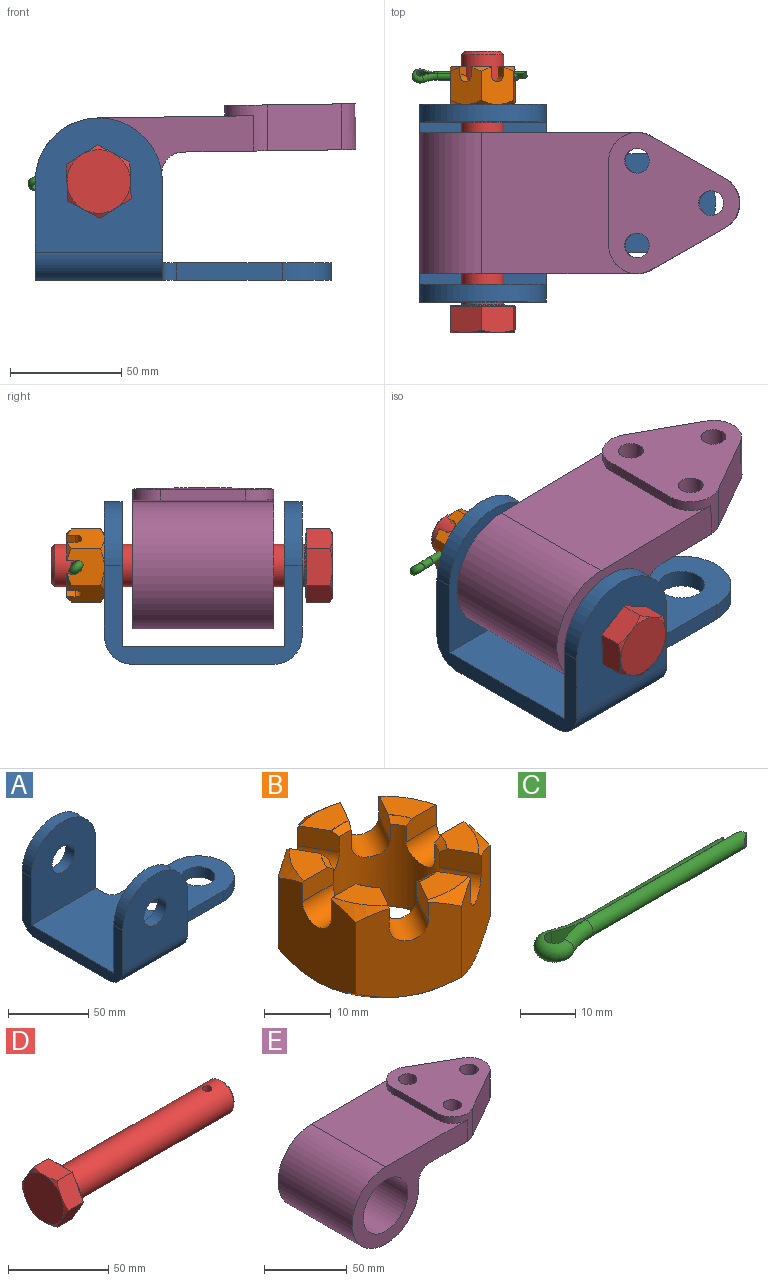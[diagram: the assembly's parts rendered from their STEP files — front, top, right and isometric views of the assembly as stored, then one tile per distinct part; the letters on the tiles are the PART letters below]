
ASSEMBLY  parts=5 mates=4
PART A: 22 faces, bbox 133.4x88.9x73 mm
  f0: plane 44.45x15.88mm, normal (1,0,0), area 381.2mm2, adj f2,f6,f7,f14,f15,f18,f21
  f1: cylinder r=9.92mm len=19.85mm, axis (0,1,0), area 494.9mm2, adj f7,f18
  f2: cylinder r=28.57mm len=57.15mm, axis (0,1,0), area 712.6mm2, adj f0,f7,f8,f18
  f3: plane 47.63x7.94mm, normal (0,-1,0), area 378mm2, adj f4,f13,f14,f15
  f4: cylinder r=22.23mm len=44.45mm, axis (0,0,-1), area 554.2mm2, adj f3,f5,f14,f15
  f5: plane 47.63x7.94mm, normal (0,1,0), area 378mm2, adj f4,f6,f14,f15
  f6: cylinder r=6.35mm len=7.94mm, axis (0,0,-1), area 79.2mm2, adj f0,f5,f14,f15
  f7: plane 60.33x57.15mm, normal (0,1,0), area 2787.8mm2, adj f0,f1,f2,f8,f21
  f8: plane 88.9x44.45mm, normal (-1,0,0), area 1216.1mm2, adj f2,f7,f9,f14,f15,f17,f18,f19
  f9: plane 60.33x57.15mm, normal (0,-1,0), area 2787.8mm2, adj f8,f10,f16,f17,f20
  f10: plane 44.45x15.88mm, normal (1,0,0), area 381.2mm2, adj f9,f13,f14,f15,f17,f19,f20
  f11: cylinder r=10.33mm len=20.65mm, axis (0,0,-1), area 514.9mm2, adj f14,f15
  f12: cylinder r=10.33mm len=20.65mm, axis (0,0,-1), area 514.9mm2, adj f14,f15
  f13: cylinder r=6.35mm len=7.94mm, axis (0,0,-1), area 79.2mm2, adj f3,f10,f14,f15
  f14: plane 133.35x73.03mm, normal (0,0,1), area 6695.9mm2, adj f0,f3,f4,f5,f6,f8,f10,f11
  f15: plane 133.35x63.5mm, normal (0,0,-1), area 6151.6mm2, adj f0,f3,f4,f5,f6,f8,f10,f11
  f16: cylinder r=9.92mm len=19.85mm, axis (0,1,0), area 494.9mm2, adj f9,f19
  f17: cylinder r=28.57mm len=57.15mm, axis (0,1,0), area 712.6mm2, adj f8,f9,f10,f19
  f18: plane 65.09x57.15mm, normal (0,-1,0), area 3060mm2, adj f0,f1,f2,f8,f14
  f19: plane 65.09x57.15mm, normal (0,1,0), area 3060mm2, adj f8,f10,f14,f16,f17
  f20: cylinder r=12.7mm len=57.15mm, axis (1,0,0), area 1140.1mm2, adj f8,f9,f10,f15
  f21: cylinder r=12.7mm len=57.15mm, axis (-1,0,0), area 1140.1mm2, adj f0,f7,f8,f15
PART B: 64 faces, bbox 33x33x16.9 mm
  f0: cylinder r=8.33mm len=16.67mm, axis (0,0,1), area 599.6mm2, adj f8,f9,f10,f11,f12,f13,f14,f15
  f1: plane 28.58x28.58mm, normal (0,0,-1), area 356.3mm2, adj f32,f33,f34,f35,f36,f37,f51
  f2: plane 8.68x4.95mm, normal (0,0,1), area 30mm2, adj f12,f16,f41,f48
  f3: plane 7.52x6.81mm, normal (0,0,1), area 30mm2, adj f9,f13,f43,f49
  f4: plane 7.52x6.81mm, normal (0,0,1), area 30mm2, adj f8,f18,f39,f44
  f5: plane 7.52x6.81mm, normal (0,0,1), area 30mm2, adj f11,f15,f42,f46
  f6: plane 7.52x6.81mm, normal (0,0,1), area 30mm2, adj f10,f17,f40,f47
  f7: plane 8.68x4.95mm, normal (0,0,1), area 30mm2, adj f14,f19,f38,f45
  f8: plane 6.56x3.71mm, normal (0,-1,0), area 23.4mm2, adj f0,f4,f22,f26,f39,f44,f62,f63
  f9: plane 6.56x3.71mm, normal (0,1,0), area 23.4mm2, adj f0,f3,f22,f26,f43,f49,f52,f53
  f10: plane 6.56x3.71mm, normal (0,1,0), area 23.4mm2, adj f0,f6,f25,f27,f40,f47,f56,f57
  f11: plane 6.56x3.71mm, normal (0,-1,0), area 23.4mm2, adj f0,f5,f25,f27,f42,f46,f58,f59
  f12: plane 5.69x3.71mm, normal (0.87,0.5,0), area 23.4mm2, adj f0,f2,f23,f28,f41,f48,f54,f55
  f13: plane 5.69x3.71mm, normal (-0.87,-0.5,0), area 23.4mm2, adj f0,f3,f23,f28,f43,f49,f52,f53
  f14: plane 5.69x3.71mm, normal (-0.87,-0.5,0), area 23.4mm2, adj f0,f7,f20,f29,f38,f45,f60,f61
  f15: plane 5.69x3.71mm, normal (0.87,0.5,0), area 23.4mm2, adj f0,f5,f20,f29,f42,f46,f58,f59
  f16: plane 5.69x3.71mm, normal (-0.87,0.5,0), area 23.4mm2, adj f0,f2,f24,f30,f41,f48,f54,f55
  f17: plane 5.69x3.71mm, normal (0.87,-0.5,0), area 23.4mm2, adj f0,f6,f24,f30,f40,f47,f56,f57
  f18: plane 5.69x3.71mm, normal (-0.87,0.5,0), area 23.4mm2, adj f0,f4,f21,f31,f39,f44,f62,f63
  f19: plane 5.69x3.71mm, normal (0.87,-0.5,0), area 23.4mm2, adj f0,f7,f21,f31,f38,f45,f60,f61
  f20: plane 16.62x14.29mm, normal (-0.5,0.87,0), area 220.6mm2, adj f14,f15,f21,f25,f29,f32,f33,f38
  f21: plane 16.62x14.29mm, normal (0.5,0.87,0), area 220.6mm2, adj f18,f19,f20,f22,f31,f33,f34,f38
  f22: plane 16.63x16.51mm, normal (1,0,0), area 220.6mm2, adj f8,f9,f21,f23,f26,f34,f35,f39
  f23: plane 16.62x14.29mm, normal (0.5,-0.87,0), area 220.6mm2, adj f12,f13,f22,f24,f28,f35,f36,f41
  f24: plane 16.62x14.29mm, normal (-0.5,-0.87,0), area 220.6mm2, adj f16,f17,f23,f25,f30,f36,f37,f40
  f25: plane 16.63x16.51mm, normal (-1,0,0), area 220.6mm2, adj f10,f11,f20,f24,f27,f32,f37,f40
  f26: cylinder r=3.05mm len=6.53mm, axis (1,0,0), area 59.8mm2, adj f0,f8,f9,f22
  f27: cylinder r=3.05mm len=6.53mm, axis (1,0,0), area 59.8mm2, adj f0,f10,f11,f25
  f28: cylinder r=3.05mm len=8.7mm, axis (-0.5,0.87,0), area 59.8mm2, adj f0,f12,f13,f23
  f29: cylinder r=3.05mm len=8.7mm, axis (-0.5,0.87,0), area 59.8mm2, adj f0,f14,f15,f20
  f30: cylinder r=3.05mm len=8.7mm, axis (0.5,0.87,0), area 59.8mm2, adj f0,f16,f17,f24
  f31: cylinder r=3.05mm len=8.7mm, axis (0.5,0.87,0), area 59.8mm2, adj f0,f18,f19,f21
  f32: cone r=14.29mm half-angle=49.2deg, axis (0,0,1), area 14.5mm2, adj f1,f20,f25
  f33: cone r=14.29mm half-angle=49.2deg, axis (0,0,1), area 14.5mm2, adj f1,f20,f21
  f34: cone r=14.29mm half-angle=49.2deg, axis (0,0,1), area 14.5mm2, adj f1,f21,f22
  f35: cone r=14.29mm half-angle=49.2deg, axis (0,0,1), area 14.5mm2, adj f1,f22,f23
  f36: cone r=14.29mm half-angle=49.2deg, axis (0,0,1), area 14.5mm2, adj f1,f23,f24
  f37: cone r=14.29mm half-angle=49.2deg, axis (0,0,1), area 14.5mm2, adj f1,f24,f25
  f38: cone r=14.29mm half-angle=49.2deg, axis (0,0,-1), area 13.6mm2, adj f7,f14,f19,f20,f21
  f39: cone r=14.29mm half-angle=49.2deg, axis (0,0,-1), area 13.6mm2, adj f4,f8,f18,f21,f22
  f40: cone r=14.29mm half-angle=49.2deg, axis (0,0,-1), area 13.6mm2, adj f6,f10,f17,f24,f25
  f41: cone r=14.29mm half-angle=49.2deg, axis (0,0,-1), area 13.6mm2, adj f2,f12,f16,f23,f24
  f42: cone r=14.29mm half-angle=49.2deg, axis (0,0,-1), area 13.6mm2, adj f5,f11,f15,f20,f25
  f43: cone r=14.29mm half-angle=49.2deg, axis (0,0,-1), area 13.6mm2, adj f3,f9,f13,f22,f23
  f44: cone r=8.21mm half-angle=55deg, axis (0,0,1), area 0.1mm2, adj f4,f8,f18,f63
  f45: cone r=8.21mm half-angle=55deg, axis (0,0,1), area 0.1mm2, adj f7,f14,f19,f60
  f46: cone r=8.21mm half-angle=55deg, axis (0,0,1), area 0.1mm2, adj f5,f11,f15,f58
  f47: cone r=8.21mm half-angle=55deg, axis (0,0,1), area 0.1mm2, adj f6,f10,f17,f56
  f48: cone r=8.21mm half-angle=55deg, axis (0,0,1), area 0.1mm2, adj f2,f12,f16,f54
  f49: cone r=8.21mm half-angle=55deg, axis (0,0,1), area 0.1mm2, adj f3,f9,f13,f52
  f50: cone r=9.53mm half-angle=55deg, axis (0,0,-1), area 81.6mm2, adj f0,f51
  f51: cylinder r=9.53mm len=19.05mm, axis (0,0,1), area 1.5mm2, adj f1,f50
  f52: cone r=9.53mm half-angle=55deg, axis (0,0,-1), area 0.1mm2, adj f9,f13,f49,f53
  f53: cone r=8.33mm half-angle=55deg, axis (0,0,1), area 4.5mm2, adj f0,f9,f13,f52
  f54: cone r=9.53mm half-angle=55deg, axis (0,0,-1), area 0.1mm2, adj f12,f16,f48,f55
  f55: cone r=8.33mm half-angle=55deg, axis (0,0,1), area 4.5mm2, adj f0,f12,f16,f54
  f56: cone r=9.53mm half-angle=55deg, axis (0,0,-1), area 0.1mm2, adj f10,f17,f47,f57
  f57: cone r=8.33mm half-angle=55deg, axis (0,0,1), area 4.5mm2, adj f0,f10,f17,f56
  f58: cone r=9.53mm half-angle=55deg, axis (0,0,-1), area 0.1mm2, adj f11,f15,f46,f59
  f59: cone r=8.33mm half-angle=55deg, axis (0,0,1), area 4.5mm2, adj f0,f11,f15,f58
  f60: cone r=9.53mm half-angle=55deg, axis (0,0,-1), area 0.1mm2, adj f14,f19,f45,f61
  f61: cone r=8.33mm half-angle=55deg, axis (0,0,1), area 4.5mm2, adj f0,f14,f19,f60
  f62: cone r=8.33mm half-angle=55deg, axis (0,0,1), area 4.5mm2, adj f0,f8,f18,f63
  f63: cone r=9.53mm half-angle=55deg, axis (0,0,-1), area 0.1mm2, adj f8,f18,f44,f62
PART C: 14 faces, bbox 52x8x3.7 mm
  f0: plane 38.67x3.7mm, normal (0,1,0), area 143.1mm2, adj f1,f2,f13
  f1: cylinder r=1.85mm len=40mm, axis (1,0,0), area 227.7mm2, adj f0,f3,f12,f13
  f2: cylinder r=16.37mm len=7.19mm, axis (0,0,-1), area 27.5mm2, adj f0,f3,f4
  f3: torus R=16.37mm, axis (0,0,-1), area 40.1mm2, adj f1,f2,f5
  f4: cylinder r=1.85mm len=3.7mm, axis (0,0,1), area 27.8mm2, adj f2,f5,f6
  f5: torus R=1.85mm, axis (0,0,1), area 71.2mm2, adj f3,f4,f7
  f6: cylinder r=16.37mm len=7.19mm, axis (0,0,-1), area 27.5mm2, adj f4,f7,f9
  f7: torus R=16.37mm, axis (0,0,-1), area 40.1mm2, adj f5,f6,f8
  f8: cylinder r=1.85mm len=36mm, axis (1,0,0), area 204.5mm2, adj f7,f9,f10,f11
  f9: plane 34.67x3.7mm, normal (0,-1,0), area 128.3mm2, adj f6,f8,f10
  f10: plane 3.7x1.33mm, normal (0.57,-0.82,0), area 5.7mm2, adj f8,f9,f11
  f11: plane 3.2x1.31mm, normal (0.58,0.82,0), area 3.6mm2, adj f8,f10
  f12: plane 3.2x1.31mm, normal (0.58,-0.82,0), area 3.6mm2, adj f1,f13
  f13: plane 3.7x1.33mm, normal (0.57,0.82,0), area 5.7mm2, adj f0,f1,f12
PART D: 26 faces, bbox 126.6x33x33 mm
  f0: plane 28.58x28.58mm, normal (1,0,0), area 325.1mm2, adj f10,f24
  f1: cylinder r=9.53mm len=112.28mm, axis (-1,0,0), area 6683.8mm2, adj f2,f24,f25
  f2: cone r=8.01mm half-angle=45deg, axis (-1,0,0), area 117.9mm2, adj f1,f3
  f3: plane 16.03x16.03mm, normal (1,0,0), area 201.7mm2, adj f2
  f4: plane 12.37x7.14mm, normal (1,0,0), area 11mm2, adj f10,f18,f23
  f5: plane 14.29x4.12mm, normal (1,0,0), area 11mm2, adj f10,f22,f23
  f6: plane 12.37x7.14mm, normal (1,0,0), area 11mm2, adj f10,f21,f22
  f7: plane 12.37x7.14mm, normal (1,0,0), area 11mm2, adj f10,f20,f21
  f8: plane 14.29x4.12mm, normal (1,0,0), area 11mm2, adj f10,f19,f20
  f9: plane 12.37x7.14mm, normal (1,0,0), area 11mm2, adj f10,f18,f19
  f10: cylinder r=14.29mm len=28.58mm, axis (-1,0,0), area 34.2mm2, adj f0,f4,f5,f6,f7,f8,f9
  f11: plane 28.58x28.58mm, normal (-1,0,0), area 641.3mm2, adj f12,f13,f14,f15,f16,f17
  f12: cone r=14.29mm half-angle=60deg, axis (1,0,0), area 12.7mm2, adj f11,f22,f23
  f13: cone r=14.29mm half-angle=60deg, axis (1,0,0), area 12.7mm2, adj f11,f21,f22
  f14: cone r=14.29mm half-angle=60deg, axis (1,0,0), area 12.7mm2, adj f11,f20,f21
  f15: cone r=14.29mm half-angle=60deg, axis (1,0,0), area 12.7mm2, adj f11,f19,f20
  f16: cone r=14.29mm half-angle=60deg, axis (1,0,0), area 12.7mm2, adj f11,f18,f23
  f17: cone r=14.29mm half-angle=60deg, axis (1,0,0), area 12.7mm2, adj f11,f18,f19
  f18: plane 16.51x11.89mm, normal (0,0,-1), area 188.9mm2, adj f4,f9,f16,f17,f19,f23
  f19: plane 14.29x11.89mm, normal (0,-0.87,-0.5), area 188.9mm2, adj f8,f9,f15,f17,f18,f20
  f20: plane 14.29x11.89mm, normal (0,-0.87,0.5), area 188.9mm2, adj f7,f8,f14,f15,f19,f21
  f21: plane 16.51x11.89mm, normal (0,0,1), area 188.9mm2, adj f6,f7,f13,f14,f20,f22
  f22: plane 14.29x11.89mm, normal (0,0.87,0.5), area 188.9mm2, adj f5,f6,f12,f13,f21,f23
  f23: plane 14.29x11.89mm, normal (0,0.87,-0.5), area 188.9mm2, adj f4,f5,f12,f16,f18,f22
  f24: torus R=10.03mm, axis (1,0,0), area 48.7mm2, adj f0,f1
  f25: cylinder r=2.38mm len=19.05mm, axis (0,0,1), area 285mm2, adj f1
PART E: 17 faces, bbox 144.5x63.5x61.9 mm
  f0: plane 77.93x63.5mm, normal (0,0,-1), area 3597.1mm2, adj f4,f5,f6,f7,f8,f9,f10,f12
  f1: plane 69.85x63.5mm, normal (0,0,1), area 3698.3mm2, adj f2,f5,f6,f10,f11,f12
  f2: cylinder r=28.57mm len=63.5mm, axis (0,1,0), area 8702.1mm2, adj f1,f4,f5,f6
  f3: cylinder r=19.05mm len=63.5mm, axis (0,1,0), area 7600.6mm2, adj f5,f6
  f4: cylinder r=9.53mm len=63.5mm, axis (0,1,0), area 1000.5mm2, adj f0,f2,f5,f6
  f5: plane 98.43x57.15mm, normal (0,-1,0), area 2273.6mm2, adj f0,f1,f2,f3,f4,f12
  f6: plane 98.43x57.15mm, normal (0,1,0), area 2273.6mm2, adj f0,f1,f2,f3,f4,f10
  f7: cylinder r=5.56mm len=20.65mm, axis (0,0,-1), area 721.7mm2, adj f0,f16
  f8: cylinder r=5.56mm len=20.65mm, axis (0,0,-1), area 721.7mm2, adj f0,f16
  f9: plane 33.35x20.65mm, normal (0.5,0.87,0), area 793.1mm2, adj f0,f10,f14,f16
  f10: cylinder r=12.7mm len=20.65mm, axis (0,0,-1), area 231.4mm2, adj f0,f1,f6,f9,f11,f16
  f11: plane 38.1x4.78mm, normal (-1,0,0), area 181.9mm2, adj f1,f10,f12,f16
  f12: cylinder r=12.7mm len=20.65mm, axis (0,0,-1), area 231.4mm2, adj f0,f1,f5,f11,f13,f16
  f13: plane 33.35x20.65mm, normal (0.5,-0.87,0), area 793.1mm2, adj f0,f12,f14,f16
  f14: cylinder r=12.7mm len=22.06mm, axis (0,0,-1), area 551.7mm2, adj f0,f9,f13,f16
  f15: cylinder r=5.56mm len=20.65mm, axis (0,0,-1), area 721.7mm2, adj f0,f16
  f16: plane 63.5x58.75mm, normal (0,0,1), area 2309.8mm2, adj f7,f8,f9,f10,f11,f12,f13,f14
PLACE A t=(-78.4,-17.02,-49.72)mm fixed
PLACE B rot(axis=(-1,-0.02,-0.02),90deg) t=(-49.82,44.32,-5.27)mm
PLACE C rot(axis=(1,-0.01,0.02),135.9deg) t=(-77.92,40.22,-6.33)mm
PLACE D rot(axis=(0.57,0.57,0.59),118.8deg) t=(-49.82,-75.24,-5.27)mm
PLACE E rot(axis=(0,-1,0),0.8deg) t=(-49.82,14.73,-5.27)mm
MATE revolute B.f0 <-> A.f1  axis (0,-1,0) through (-49.82,27.43,-5.27)mm
MATE revolute B.f0 <-> D.f1  axis (0,1,0) through (-49.82,43.47,-5.27)mm
MATE revolute C.f1 <-> D.f25  axis (1,0,0.04) through (-49.82,40.22,-5.27)mm
MATE revolute E.f2 <-> A.f1  axis (0,1,0) through (-49.82,-17.02,-5.27)mm
